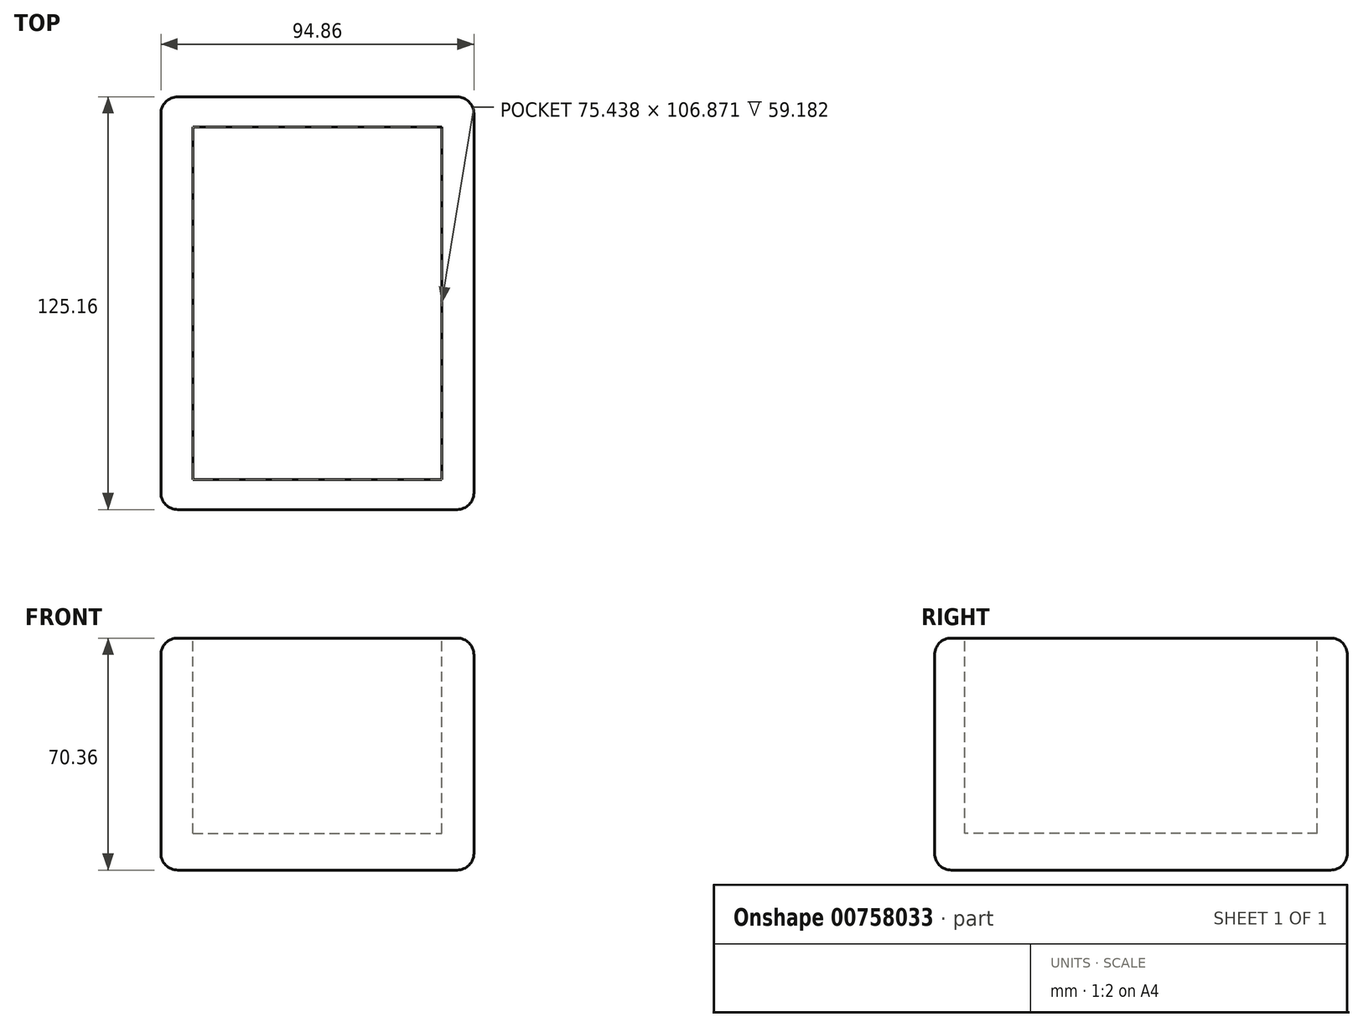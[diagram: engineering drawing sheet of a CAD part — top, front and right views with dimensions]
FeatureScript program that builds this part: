
annotation { "Feature Type Name" : "Feature", "Feature Type Description" : "" }
export const myFeature = defineFeature(function(context is Context, id is Id, definition is map)
    precondition{}
    {
        {
            var Q0;
            Q0=qCreatedBy(makeId("Top.planeOp"),FACE);
            var sketch = newSketch(context, id + "F0", { "sketchPlane" : qUnion([Q0])});
            skLineSegment(sketch, "E0.bottom", {"start": v(-47.43, 62.58) * mm, "end": v(47.43, 62.58) * mm});
            skLineSegment(sketch, "E0.top", {"start": v(-47.43, -62.58) * mm, "end": v(47.43, -62.58) * mm});
            skLineSegment(sketch, "E0.left", {"start": v(-47.43, 62.58) * mm, "end": v(-47.43, -62.58) * mm});
            skLineSegment(sketch, "E0.right", {"start": v(47.43, 62.58) * mm, "end": v(47.43, -62.58) * mm});
            skPoint(sketch, "E0.middle", {"position": v(0, 0) * mm});
            skSolve(sketch);
        }
        {
            var Q0;
            Q0=makeQuery(id+"F0.imprint","IMPRINT",FACE,{"disambiguationData":[TD([[makeQuery(id+"F0.imprint","IMPRINT",EDGE,{"derivedFrom":sQuery(id+"F0.wireOp",EDGE,"E0.bottom")}),-1.0]])]});
            extrude(context, id + "F1", {"entities" : qUnion([Q0]), "depth" : 70.36 * mm, "offsetDistance" : 25.4 * mm});
        }
        {
            var Q0;
            Q0=makeQuery(id+"F1.opExtrude","CAP_FACE",FACE,{"disambiguationData":[OSD([sQuery(id+"F0.wireOp",EDGE,"E0.bottom"),sQuery(id+"F0.wireOp",EDGE,"E0.top"),sQuery(id+"F0.wireOp",EDGE,"E0.left"),sQuery(id+"F0.wireOp",EDGE,"E0.right")])],"isStart":false});
            var sketch = newSketch(context, id + "F2", { "sketchPlane" : qUnion([Q0])});
            skLineSegment(sketch, "E1.bottom", {"start": v(-37.72, 53.44) * mm, "end": v(37.72, 53.44) * mm});
            skLineSegment(sketch, "E1.top", {"start": v(-37.72, -53.44) * mm, "end": v(37.72, -53.44) * mm});
            skLineSegment(sketch, "E1.left", {"start": v(-37.72, 53.44) * mm, "end": v(-37.72, -53.44) * mm});
            skLineSegment(sketch, "E1.right", {"start": v(37.72, 53.44) * mm, "end": v(37.72, -53.44) * mm});
            skPoint(sketch, "E1.middle", {"position": v(0, 0) * mm});
            skSolve(sketch);
        }
        {
            var Q0;
            Q0=makeQuery(id+"F2.imprint","IMPRINT",FACE,{"disambiguationData":[TD([[makeQuery(id+"F2.imprint","IMPRINT",EDGE,{"derivedFrom":sQuery(id+"F2.wireOp",EDGE,"E1.bottom")}),-1.0]])]});
            extrude(context, id + "F3", {"entities" : qUnion([Q0]), "operationType" : NewBodyOperationType.REMOVE, "oppositeDirection" : true, "depth" : 59.18 * mm, "offsetDistance" : 25.4 * mm});
        }
        {
            var Q0;
            Q0=makeQuery(id+"F1.opExtrude","SWEPT_EDGE",EDGE,{"disambiguationData":[OSD([sQuery(id+"F0.wireOp",EDGE,"E0.bottom"),sQuery(id+"F0.wireOp",EDGE,"E0.right")])]});
            var Q1;
            Q1=makeQuery(id+"F1.opExtrude","CAP_EDGE",EDGE,{"disambiguationData":[OSD([sQuery(id+"F0.wireOp",EDGE,"E0.bottom")])],"isStart":false});
            var Q2;
            Q2=makeQuery(id+"F1.opExtrude","CAP_EDGE",EDGE,{"disambiguationData":[OSD([sQuery(id+"F0.wireOp",EDGE,"E0.left")])],"isStart":false});
            var Q3;
            Q3=makeQuery(id+"F1.opExtrude","CAP_EDGE",EDGE,{"disambiguationData":[OSD([sQuery(id+"F0.wireOp",EDGE,"E0.top")])],"isStart":false});
            var Q4;
            Q4=makeQuery(id+"F1.opExtrude","SWEPT_FACE",FACE,{"disambiguationData":[OSD([sQuery(id+"F0.wireOp",EDGE,"E0.right")])]});
            var Q5;
            Q5=makeQuery(id+"F1.opExtrude","SWEPT_FACE",FACE,{"disambiguationData":[OSD([sQuery(id+"F0.wireOp",EDGE,"E0.top")])]});
            var Q6;
            Q6=makeQuery(id+"F1.opExtrude","SWEPT_FACE",FACE,{"disambiguationData":[OSD([sQuery(id+"F0.wireOp",EDGE,"E0.left")])]});
            var Q7;
            Q7=makeQuery(id+"F1.opExtrude","SWEPT_FACE",FACE,{"disambiguationData":[OSD([sQuery(id+"F0.wireOp",EDGE,"E0.bottom")])]});
            fillet(context, id + "F4", {"entities" : qUnion([Q0, Q1, Q2, Q3, Q4, Q5, Q6, Q7]), "radius" : 5.08 * mm, "tangentPropagation" : true, "allowEdgeOverflow" : false});
        }
    });
